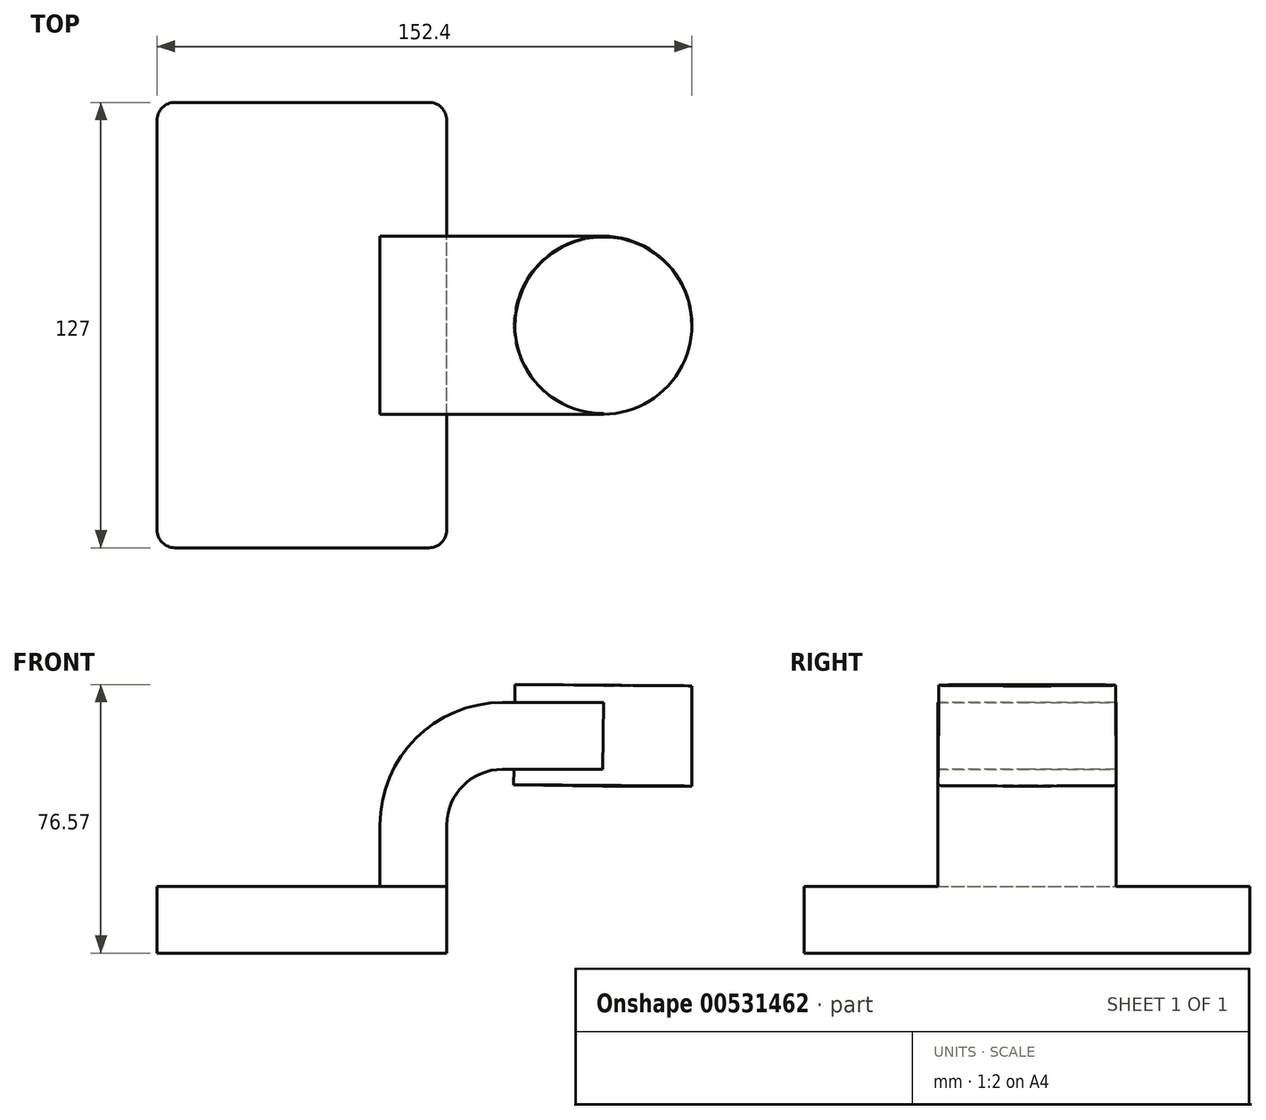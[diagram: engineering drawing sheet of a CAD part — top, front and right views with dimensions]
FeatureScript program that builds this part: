
annotation { "Feature Type Name" : "Feature", "Feature Type Description" : "" }
export const myFeature = defineFeature(function(context is Context, id is Id, definition is map)
    precondition{}
    {
        {
            var Q0;
            Q0=qCreatedBy(makeId("Front.planeOp"),FACE);
            var sketch = newSketch(context, id + "F0", { "sketchPlane" : qUnion([Q0])});
            skLineSegment(sketch, "E0.bottom", {"start": v(-41.28, -9.52) * mm, "end": v(41.27, -9.52) * mm});
            skLineSegment(sketch, "E0.top", {"start": v(-41.28, 9.53) * mm, "end": v(41.27, 9.53) * mm});
            skLineSegment(sketch, "E0.left", {"start": v(-41.28, -9.52) * mm, "end": v(-41.28, 9.53) * mm});
            skLineSegment(sketch, "E0.right", {"start": v(41.27, -9.52) * mm, "end": v(41.27, 9.53) * mm});
            skPoint(sketch, "E0.middle", {"position": v(0, 0) * mm});
            skLineSegment(sketch, "E1.bottom", {"start": v(111.12, 38.1) * mm, "end": v(60.32, 38.1) * mm});
            skLineSegment(sketch, "E1.top", {"start": v(111.12, 66.68) * mm, "end": v(60.32, 66.68) * mm});
            skLineSegment(sketch, "E1.left", {"start": v(111.12, 38.1) * mm, "end": v(111.12, 66.68) * mm});
            skLineSegment(sketch, "E1.right", {"start": v(60.32, 38.1) * mm, "end": v(60.32, 66.67) * mm});
            skPoint(sketch, "E1.middle", {"position": v(85.72, 52.39) * mm});
            skLineSegment(sketch, "E2", {"start": v(41.27, 9.53) * mm, "end": v(41.27, 27) * mm});
            skArc(sketch, "E3", {"start": v(41.27, 27) * mm, "mid": v(45.92, 38.23) * mm, "end": v(57.15, 42.88) * mm});
            skLineSegment(sketch, "E4", {"start": v(57.15, 42.88) * mm, "end": v(85.93, 42.88) * mm});
            skLineSegment(sketch, "E5.0", {"start": v(57.15, 61.93) * mm, "end": v(85.93, 61.93) * mm});
            skArc(sketch, "E5.1", {"start": v(22.22, 27) * mm, "mid": v(32.45, 51.7) * mm, "end": v(57.15, 61.93) * mm});
            skLineSegment(sketch, "E5.2", {"start": v(22.22, 9.53) * mm, "end": v(22.22, 27) * mm});
            skLineSegment(sketch, "E6", {"start": v(85.72, 38.1) * mm, "end": v(85.93, 66.68) * mm});
            skFitSpline(sketch, "E7", {"points": [v(-41.28, 9.53) * mm, v(57.15, 61.93) * mm], "startDerivative": vector(-2.24, 113.78) * mm, "endDerivative": vector(171.45, -6.15) * mm});
            skSolve(sketch);
        }
        {
            var Q0;
            Q0=makeQuery(id+"F0.imprint","IMPRINT",FACE,{"disambiguationData":[TD([[makeQuery(id+"F0.imprint","IMPRINT",EDGE,{"derivedFrom":sQuery(id+"F0.wireOp",EDGE,"E0.bottom")}),1.0]])]});
            extrude(context, id + "F1", {"entities" : qUnion([Q0]), "endBound" : BoundingType.SYMMETRIC, "depth" : 127 * mm, "offsetDistance" : 25.4 * mm});
        }
        {
            var Q0;
            {var subQ1=sQuery(id+"F0.wireOp",EDGE,"E2");Q0=makeQuery(id+"F0.imprint","IMPRINT",FACE,{"disambiguationData":[TD([[makeQuery(id+"F0.imprint","IMPRINT",EDGE,{"derivedFrom":subQ1}),1.0]])]});}
            var Q1;
            {var subQ0=sQuery(id+"F0.wireOp",EDGE,"E4");var subQ1=sQuery(id+"F0.wireOp",EDGE,"E1.right");var subQ2=makeQuery(id+"F0.imprint","INTERSECT",VERTEX,{"derivedFrom":[subQ1,subQ0]});Q1=makeQuery(id+"F0.imprint","IMPRINT",FACE,{"disambiguationData":[TD([[makeQuery(id+"F0.imprint","IMPRINT",EDGE,{"disambiguationData":[TD([[subQ2,-1.0]])],"derivedFrom":subQ1}),-1.0]])]});}
            extrude(context, id + "F2", {"entities" : qUnion([Q0, Q1]), "operationType" : NewBodyOperationType.ADD, "endBound" : BoundingType.SYMMETRIC, "depth" : 50.8 * mm, "offsetDistance" : 25.4 * mm});
        }
        {
            var Q0;
            Q0=makeQuery(id+"F0.imprint","IMPRINT",FACE,{"disambiguationData":[TD([[makeQuery(id+"F0.imprint","IMPRINT",EDGE,{"derivedFrom":sQuery(id+"F0.wireOp",EDGE,"E5.1")}),1.0]])]});
            extrude(context, id + "F3", {"entities" : qUnion([Q0]), "operationType" : NewBodyOperationType.ADD, "endBound" : BoundingType.SYMMETRIC, "depth" : 15.88 * mm, "offsetDistance" : 25.4 * mm});
        }
        {
            var Q0;
            {var subQ4=sQuery(id+"F0.wireOp",EDGE,"E1.left");Q0=makeQuery(id+"F0.imprint","IMPRINT",FACE,{"disambiguationData":[TD([[makeQuery(id+"F0.imprint","IMPRINT",EDGE,{"derivedFrom":subQ4}),1.0]])]});}
            var Q1;
            Q1=sQuery(id+"F0.wireOp",EDGE,"E6");
            revolve(context, id + "F4", {"operationType" : NewBodyOperationType.ADD, "entities" : qUnion([Q0]), "axis" : qUnion([Q1]), "revolveType" : RevolveType.FULL});
        }
        {
            var Q0;
            Q0=makeQuery(id+"F1.opExtrude","CAP_EDGE",EDGE,{"disambiguationData":[OSD([sQuery(id+"F0.wireOp",EDGE,"E0.right")])],"isStart":true});
            var Q1;
            Q1=makeQuery(id+"F1.opExtrude","CAP_EDGE",EDGE,{"disambiguationData":[OSD([sQuery(id+"F0.wireOp",EDGE,"E0.right")])],"isStart":false});
            var Q2;
            Q2=makeQuery(id+"F1.opExtrude","CAP_EDGE",EDGE,{"disambiguationData":[OSD([sQuery(id+"F0.wireOp",EDGE,"E0.left")])],"isStart":false});
            var Q3;
            Q3=makeQuery(id+"F1.opExtrude","CAP_EDGE",EDGE,{"disambiguationData":[OSD([sQuery(id+"F0.wireOp",EDGE,"E0.left")])],"isStart":true});
            var Q4;
            {var subQ0=sQuery(id+"F0.wireOp",EDGE,"E7");var subQ1=sQuery(id+"F0.wireOp",EDGE,"E5.2");var subQ2=sQuery(id+"F0.wireOp",EDGE,"E5.1");var subQ3=sQuery(id+"F0.wireOp",EDGE,"E0.top");var subQ4=sQuery(id+"F0.wireOp",EDGE,"E5.0");Q4=makeQuery(id+"F3.boolean.opBoolean","SPLIT",EDGE,{"disambiguationData":[TD([makeQuery(id+"F3.opExtrude","CAP_FACE",FACE,{"disambiguationData":[OSD([subQ3,subQ2,subQ1,subQ0])],"isStart":false})])],"derivedFrom":makeQuery(id+"F2.opExtrude","SWEPT_EDGE",EDGE,{"disambiguationData":[OSD([subQ4,subQ2,subQ0])]})});}
            var Q5;
            {var subQ0=sQuery(id+"F0.wireOp",EDGE,"E7");var subQ1=sQuery(id+"F0.wireOp",EDGE,"E5.2");var subQ2=sQuery(id+"F0.wireOp",EDGE,"E5.1");var subQ3=sQuery(id+"F0.wireOp",EDGE,"E0.top");var subQ4=sQuery(id+"F0.wireOp",EDGE,"E5.0");Q5=makeQuery(id+"F3.boolean.opBoolean","SPLIT",EDGE,{"disambiguationData":[TD([makeQuery(id+"F3.opExtrude","CAP_FACE",FACE,{"disambiguationData":[OSD([subQ3,subQ2,subQ1,subQ0])],"isStart":true})])],"derivedFrom":makeQuery(id+"F2.opExtrude","SWEPT_EDGE",EDGE,{"disambiguationData":[OSD([subQ4,subQ2,subQ0])]})});}
            var Q6;
            Q6=makeQuery(id+"F3.opExtrude","SWEPT_FACE",FACE,{"disambiguationData":[OSD([sQuery(id+"F0.wireOp",EDGE,"E7")])]});
            fillet(context, id + "F5", {"entities" : qUnion([Q0, Q1, Q2, Q3, Q4, Q5, Q6]), "radius" : 5.08 * mm, "tangentPropagation" : true, "allowEdgeOverflow" : false});
        }
    });
